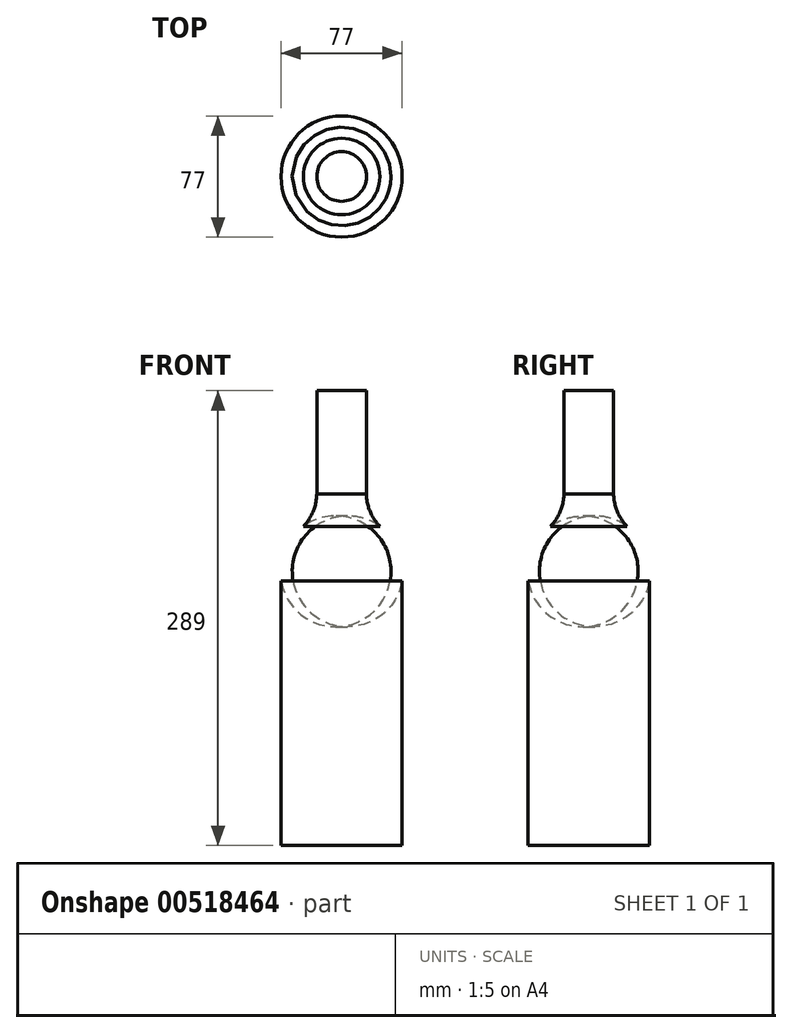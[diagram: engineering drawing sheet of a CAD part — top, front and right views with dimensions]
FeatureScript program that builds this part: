
annotation { "Feature Type Name" : "Feature", "Feature Type Description" : "" }
export const myFeature = defineFeature(function(context is Context, id is Id, definition is map)
    precondition{}
    {
        {
            var Q0;
            Q0=qCreatedBy(makeId("Right.planeOp"),FACE);
            var sketch = newSketch(context, id + "F0", { "sketchPlane" : qUnion([Q0])});
            skLineSegment(sketch, "E0", {"start": v(-104.63, 42.27) * mm, "end": v(-104.63, 331.27) * mm});
            skLineSegment(sketch, "E1", {"start": v(-104.63, 42.27) * mm, "end": v(-66.13, 42.27) * mm});
            skLineSegment(sketch, "E2", {"start": v(-66.13, 42.27) * mm, "end": v(-66.13, 210.34) * mm});
            skArc(sketch, "E3", {"start": v(-66.13, 210.34) * mm, "mid": v(-68.21, 229.79) * mm, "end": v(-80.35, 245.12) * mm});
            skArc(sketch, "E4", {"start": v(-88.88, 265.58) * mm, "mid": v(-86.53, 254.55) * mm, "end": v(-80.35, 245.12) * mm});
            skLineSegment(sketch, "E5", {"start": v(-88.88, 265.58) * mm, "end": v(-88.88, 331.27) * mm});
            skLineSegment(sketch, "E6", {"start": v(-88.88, 331.27) * mm, "end": v(-104.63, 331.27) * mm});
            skSolve(sketch);
        }
        {
            var Q0;
            Q0 = qSketchRegion(id + "F0", true);
            var Q1;
            Q1=sQuery(id+"F0.wireOp",EDGE,"E0");
            revolve(context, id + "F1", {"entities" : qUnion([Q0]), "axis" : qUnion([Q1]), "revolveType" : RevolveType.FULL});
        }
    });
